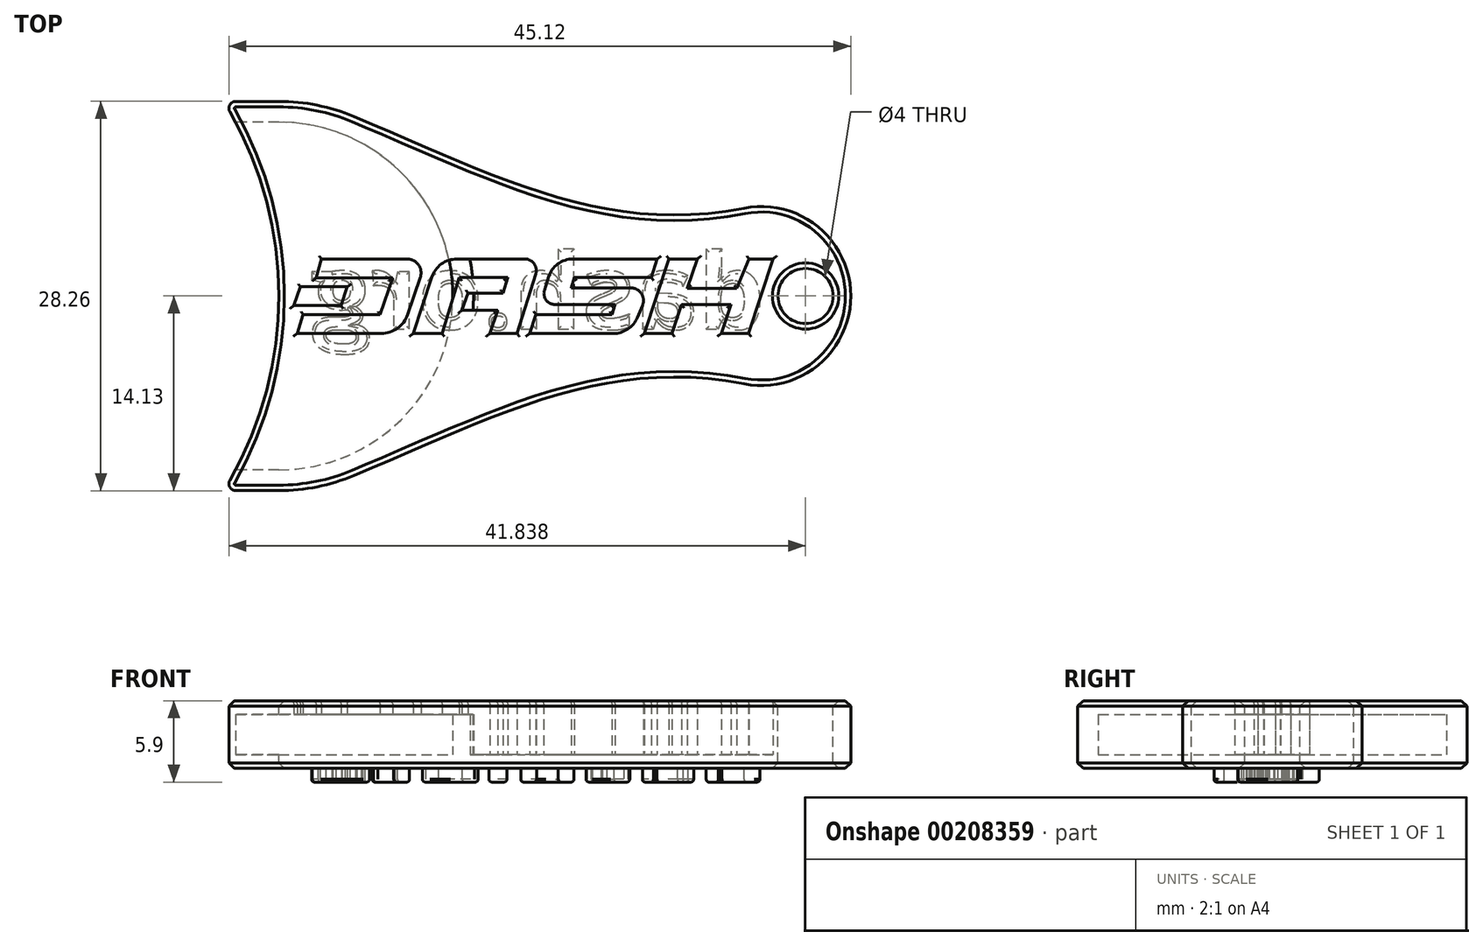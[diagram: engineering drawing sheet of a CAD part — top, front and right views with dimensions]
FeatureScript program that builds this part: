
annotation { "Feature Type Name" : "Feature", "Feature Type Description" : "" }
export const myFeature = defineFeature(function(context is Context, id is Id, definition is map)
    precondition{}
    {
        {
            var Q0;
            Q0=qCreatedBy(makeId("Top.planeOp"),FACE);
            var sketch = newSketch(context, id + "F0", { "sketchPlane" : qUnion([Q0])});
            skArc(sketch, "E0", {"start": v(0, -12.12) * mm, "mid": v(12.12, 0) * mm, "end": v(0, 12.12) * mm, "construction": true});
            skArc(sketch, "E1", {"start": v(0, -12.62) * mm, "mid": v(12.62, 0) * mm, "end": v(0, 12.62) * mm});
            skArc(sketch, "E2.0", {"start": v(0, -14.12) * mm, "mid": v(14.12, 0) * mm, "end": v(0, 14.12) * mm});
            skLineSegment(sketch, "E3", {"start": v(0, 15.93) * mm, "end": v(0, -15.93) * mm, "construction": true});
            skLineSegment(sketch, "E4", {"start": v(0, 14.12) * mm, "end": v(-3.12, 14.12) * mm});
            skLineSegment(sketch, "E5", {"start": v(0, -14.12) * mm, "end": v(-3.12, -14.12) * mm});
            skArc(sketch, "E6", {"start": v(-3.56, -13.38) * mm, "mid": v(0, 0) * mm, "end": v(-3.56, 13.38) * mm});
            skLineSegment(sketch, "E7", {"start": v(0, 12.62) * mm, "end": v(-3.14, 12.62) * mm});
            skLineSegment(sketch, "E8", {"start": v(0, -12.62) * mm, "end": v(-3.14, -12.62) * mm});
            skLineSegment(sketch, "E9", {"start": v(0, 0) * mm, "end": v(35, 0) * mm, "construction": true});
            skArc(sketch, "E10", {"start": v(33.74, -6.38) * mm, "mid": v(41.5, 0) * mm, "end": v(33.74, 6.38) * mm});
            skFitSpline(sketch, "E11", {"points": [v(33.74, 6.38) * mm, v(5.45, 13.03) * mm], "startDerivative": vector(-30.42, -5.99) * mm, "endDerivative": vector(-30.88, 12.92) * mm});
            skFitSpline(sketch, "E12.MirrorCS", {"points": [v(33.74, -6.38) * mm, v(5.45, -13.03) * mm], "startDerivative": vector(-30.42, 5.99) * mm, "endDerivative": vector(-30.88, -12.92) * mm});
            skCircle(sketch, "E13", {"center": v(38.22, 0) * mm, "radius": 2 * mm});
            skPoint(sketch, "E14.visualSharp", {"position": v(-4, 14.12) * mm});
            skArc(sketch, "E14.filletArc", {"start": v(-3.12, 14.12) * mm, "mid": v(-3.55, 13.88) * mm, "end": v(-3.56, 13.38) * mm});
            skPoint(sketch, "E15.visualSharp", {"position": v(-4, -14.12) * mm});
            skArc(sketch, "E15.filletArc", {"start": v(-3.56, -13.38) * mm, "mid": v(-3.55, -13.88) * mm, "end": v(-3.12, -14.12) * mm});
            skLineSegment(sketch, "E16", {"start": v(3.1, 2.69) * mm, "end": v(9.3, 2.69) * mm});
            skLineSegment(sketch, "E17", {"start": v(10.27, 1.35) * mm, "end": v(9.35, -1.34) * mm});
            skLineSegment(sketch, "E18", {"start": v(7.42, -2.72) * mm, "end": v(1.33, -2.72) * mm});
            skLineSegment(sketch, "E19", {"start": v(1.33, -2.72) * mm, "end": v(1.76, -1.34) * mm});
            skLineSegment(sketch, "E20", {"start": v(1.76, -1.34) * mm, "end": v(7.35, -1.34) * mm});
            skLineSegment(sketch, "E21", {"start": v(7.35, -1.34) * mm, "end": v(8.25, 1.3) * mm});
            skLineSegment(sketch, "E22", {"start": v(8.25, 1.3) * mm, "end": v(2.7, 1.3) * mm});
            skLineSegment(sketch, "E23", {"start": v(2.7, 1.3) * mm, "end": v(3.1, 2.69) * mm});
            skLineSegment(sketch, "E24", {"start": v(1.57, 0.67) * mm, "end": v(4.97, 0.67) * mm});
            skLineSegment(sketch, "E25", {"start": v(4.97, 0.67) * mm, "end": v(4.5, -0.7) * mm});
            skLineSegment(sketch, "E26", {"start": v(4.5, -0.7) * mm, "end": v(1.1, -0.7) * mm});
            skLineSegment(sketch, "E27", {"start": v(1.1, -0.7) * mm, "end": v(1.57, 0.67) * mm});
            skPoint(sketch, "E28.visualSharp", {"position": v(10.72, 2.69) * mm});
            skArc(sketch, "E28.filletArc", {"start": v(10.27, 1.35) * mm, "mid": v(10.13, 2.27) * mm, "end": v(9.3, 2.69) * mm});
            skPoint(sketch, "E29.visualSharp", {"position": v(8.88, -2.72) * mm});
            skArc(sketch, "E29.filletArc", {"start": v(7.42, -2.72) * mm, "mid": v(8.6, -2.34) * mm, "end": v(9.35, -1.34) * mm});
            skLineSegment(sketch, "E30", {"start": v(9.76, -2.72) * mm, "end": v(11.09, 1.35) * mm});
            skLineSegment(sketch, "E31", {"start": v(12.94, 2.69) * mm, "end": v(17.85, 2.69) * mm});
            skLineSegment(sketch, "E32", {"start": v(18.64, 1.61) * mm, "end": v(17.29, -2.72) * mm});
            skLineSegment(sketch, "E33", {"start": v(17.29, -2.72) * mm, "end": v(15.32, -2.72) * mm});
            skLineSegment(sketch, "E34", {"start": v(15.32, -2.72) * mm, "end": v(15.88, -1.04) * mm});
            skLineSegment(sketch, "E35", {"start": v(15.88, -1.04) * mm, "end": v(13.3, -1.04) * mm});
            skLineSegment(sketch, "E36", {"start": v(13.3, -1.04) * mm, "end": v(13.73, 0.21) * mm});
            skLineSegment(sketch, "E37", {"start": v(13.73, 0.21) * mm, "end": v(16.26, 0.21) * mm});
            skLineSegment(sketch, "E38", {"start": v(16.26, 0.21) * mm, "end": v(16.6, 1.34) * mm});
            skLineSegment(sketch, "E39", {"start": v(16.6, 1.34) * mm, "end": v(13.1, 1.34) * mm});
            skLineSegment(sketch, "E40", {"start": v(13.1, 1.34) * mm, "end": v(11.85, -2.72) * mm});
            skLineSegment(sketch, "E41", {"start": v(11.85, -2.72) * mm, "end": v(9.76, -2.72) * mm});
            skPoint(sketch, "E42.visualSharp", {"position": v(11.52, 2.69) * mm});
            skArc(sketch, "E42.filletArc", {"start": v(12.94, 2.69) * mm, "mid": v(11.8, 2.32) * mm, "end": v(11.09, 1.35) * mm});
            skPoint(sketch, "E43.visualSharp", {"position": v(18.98, 2.69) * mm});
            skArc(sketch, "E43.filletArc", {"start": v(18.64, 1.61) * mm, "mid": v(18.52, 2.35) * mm, "end": v(17.85, 2.69) * mm});
            skLineSegment(sketch, "E44", {"start": v(18.2, -2.72) * mm, "end": v(24.25, -2.72) * mm});
            skLineSegment(sketch, "E45", {"start": v(26.01, -1.56) * mm, "end": v(26.39, -0.69) * mm});
            skLineSegment(sketch, "E46", {"start": v(25.54, 0.6) * mm, "end": v(21.2, 0.6) * mm});
            skLineSegment(sketch, "E47", {"start": v(21.2, 0.6) * mm, "end": v(21.44, 1.33) * mm});
            skLineSegment(sketch, "E48", {"start": v(21.44, 1.33) * mm, "end": v(27.03, 1.33) * mm});
            skLineSegment(sketch, "E49", {"start": v(27.03, 1.33) * mm, "end": v(27.45, 2.69) * mm});
            skLineSegment(sketch, "E50", {"start": v(27.45, 2.69) * mm, "end": v(21.35, 2.69) * mm});
            skLineSegment(sketch, "E51", {"start": v(19.56, 1.38) * mm, "end": v(19.27, 0.43) * mm});
            skLineSegment(sketch, "E52", {"start": v(20.04, -0.61) * mm, "end": v(24.4, -0.61) * mm});
            skLineSegment(sketch, "E53", {"start": v(24.4, -0.61) * mm, "end": v(24.18, -1.34) * mm});
            skLineSegment(sketch, "E54", {"start": v(24.18, -1.34) * mm, "end": v(18.66, -1.34) * mm});
            skLineSegment(sketch, "E55", {"start": v(18.66, -1.34) * mm, "end": v(18.2, -2.72) * mm});
            skPoint(sketch, "E56.visualSharp", {"position": v(19.97, 2.69) * mm});
            skArc(sketch, "E56.filletArc", {"start": v(21.35, 2.69) * mm, "mid": v(20.24, 2.33) * mm, "end": v(19.56, 1.38) * mm});
            skPoint(sketch, "E57.visualSharp", {"position": v(18.94, -0.61) * mm});
            skArc(sketch, "E57.filletArc", {"start": v(19.27, 0.43) * mm, "mid": v(19.39, -0.28) * mm, "end": v(20.04, -0.61) * mm});
            skPoint(sketch, "E58.visualSharp", {"position": v(26.93, 0.6) * mm});
            skArc(sketch, "E58.filletArc", {"start": v(26.39, -0.69) * mm, "mid": v(26.3, 0.18) * mm, "end": v(25.54, 0.6) * mm});
            skPoint(sketch, "E59.visualSharp", {"position": v(25.52, -2.72) * mm});
            skArc(sketch, "E59.filletArc", {"start": v(24.25, -2.72) * mm, "mid": v(25.3, -2.4) * mm, "end": v(26.01, -1.56) * mm});
            skLineSegment(sketch, "E60", {"start": v(26.52, -2.72) * mm, "end": v(28.3, 2.69) * mm});
            skLineSegment(sketch, "E61", {"start": v(28.3, 2.69) * mm, "end": v(30.35, 2.69) * mm});
            skLineSegment(sketch, "E62", {"start": v(30.35, 2.69) * mm, "end": v(29.64, 0.57) * mm});
            skLineSegment(sketch, "E63", {"start": v(29.64, 0.57) * mm, "end": v(33.2, 0.57) * mm});
            skLineSegment(sketch, "E64", {"start": v(33.2, 0.57) * mm, "end": v(34.1, 2.69) * mm});
            skLineSegment(sketch, "E65", {"start": v(34.1, 2.69) * mm, "end": v(35.84, 2.69) * mm});
            skLineSegment(sketch, "E66", {"start": v(35.84, 2.69) * mm, "end": v(34.09, -2.72) * mm});
            skLineSegment(sketch, "E67", {"start": v(34.09, -2.72) * mm, "end": v(32.1, -2.72) * mm});
            skLineSegment(sketch, "E68", {"start": v(32.1, -2.72) * mm, "end": v(32.82, -0.64) * mm});
            skLineSegment(sketch, "E69", {"start": v(32.82, -0.64) * mm, "end": v(29.23, -0.64) * mm});
            skLineSegment(sketch, "E70", {"start": v(29.23, -0.64) * mm, "end": v(28.53, -2.72) * mm});
            skLineSegment(sketch, "E71", {"start": v(28.53, -2.72) * mm, "end": v(26.52, -2.72) * mm});
            skSolve(sketch);
        }
        {
            var Q0;
            {var subQ5=sQuery(id+"F0.wireOp",EDGE,"E7");Q0=makeQuery(id+"F0.imprint","IMPRINT",FACE,{"disambiguationData":[TD([[makeQuery(id+"F0.imprint","IMPRINT",EDGE,{"derivedFrom":subQ5}),1.0]])]});}
            var Q1;
            {var subQ4=sQuery(id+"F0.wireOp",EDGE,"E5");Q1=makeQuery(id+"F0.imprint","IMPRINT",FACE,{"disambiguationData":[TD([[makeQuery(id+"F0.imprint","IMPRINT",EDGE,{"derivedFrom":subQ4}),-1.0]])]});}
            var Q2;
            {var subQ5=sQuery(id+"F0.wireOp",EDGE,"E38");Q2=makeQuery(id+"F0.imprint","IMPRINT",FACE,{"disambiguationData":[TD([[makeQuery(id+"F0.imprint","IMPRINT",EDGE,{"derivedFrom":subQ5}),1.0]])]});}
            var Q3;
            {var subQ0=sQuery(id+"F0.wireOp",EDGE,"E4");Q3=makeQuery(id+"F0.imprint","IMPRINT",FACE,{"disambiguationData":[TD([[makeQuery(id+"F0.imprint","IMPRINT",EDGE,{"derivedFrom":subQ0}),1.0]])]});}
            var Q4;
            {var subQ5=sQuery(id+"F0.wireOp",EDGE,"E36");Q4=makeQuery(id+"F0.imprint","IMPRINT",FACE,{"disambiguationData":[TD([[makeQuery(id+"F0.imprint","IMPRINT",EDGE,{"derivedFrom":subQ5}),-1.0]])]});}
            var Q5;
            {var subQ6=sQuery(id+"F0.wireOp",EDGE,"E30");Q5=makeQuery(id+"F0.imprint","IMPRINT",FACE,{"disambiguationData":[TD([[makeQuery(id+"F0.imprint","IMPRINT",EDGE,{"derivedFrom":subQ6}),-1.0]])]});}
            var Q6;
            Q6=makeQuery(id+"F0.imprint","IMPRINT",FACE,{"disambiguationData":[TD([[makeQuery(id+"F0.imprint","IMPRINT",EDGE,{"derivedFrom":sQuery(id+"F0.wireOp",EDGE,"E32")}),-1.0]])]});
            var Q7;
            {var subQ0=sQuery(id+"F0.wireOp",EDGE,"E40");var subQ9=sQuery(id+"F0.wireOp",EDGE,"E1");var subQ10=makeQuery(id+"F0.imprint","INTERSECT",VERTEX,{"derivedFrom":[subQ9,subQ0]});Q7=makeQuery(id+"F0.imprint","IMPRINT",FACE,{"disambiguationData":[TD([[makeQuery(id+"F0.imprint","IMPRINT",EDGE,{"disambiguationData":[TD([[subQ10,-1.0]])],"derivedFrom":subQ9}),-1.0]])]});}
            var Q8;
            Q8=makeQuery(id+"F0.imprint","IMPRINT",FACE,{"disambiguationData":[TD([[makeQuery(id+"F0.imprint","IMPRINT",EDGE,{"derivedFrom":sQuery(id+"F0.wireOp",EDGE,"E10")}),1.0]])]});
            var Q9;
            Q9=makeQuery(id+"F0.imprint","IMPRINT",FACE,{"disambiguationData":[TD([[makeQuery(id+"F0.imprint","IMPRINT",EDGE,{"derivedFrom":sQuery(id+"F0.wireOp",EDGE,"E16")}),-1.0]])]});
            var Q10;
            Q10=makeQuery(id+"F0.imprint","IMPRINT",FACE,{"disambiguationData":[TD([[makeQuery(id+"F0.imprint","IMPRINT",EDGE,{"derivedFrom":sQuery(id+"F0.wireOp",EDGE,"E24")}),-1.0]])]});
            var Q11;
            Q11=makeQuery(id+"F0.imprint","IMPRINT",FACE,{"disambiguationData":[TD([[makeQuery(id+"F0.imprint","IMPRINT",EDGE,{"derivedFrom":sQuery(id+"F0.wireOp",EDGE,"E44")}),1.0]])]});
            var Q12;
            Q12=makeQuery(id+"F0.imprint","IMPRINT",FACE,{"disambiguationData":[TD([[makeQuery(id+"F0.imprint","IMPRINT",EDGE,{"derivedFrom":sQuery(id+"F0.wireOp",EDGE,"E60")}),-1.0]])]});
            extrude(context, id + "F1", {"entities" : qUnion([Q0, Q1, Q2, Q3, Q4, Q5, Q6, Q7, Q8, Q9, Q10, Q11, Q12]), "oppositeDirection" : true, "depth" : 1 * mm});
        }
        {
            var Q0;
            {var subQ0=sQuery(id+"F0.wireOp",EDGE,"E4");Q0=makeQuery(id+"F0.imprint","IMPRINT",FACE,{"disambiguationData":[TD([[makeQuery(id+"F0.imprint","IMPRINT",EDGE,{"derivedFrom":subQ0}),1.0]])]});}
            var Q1;
            {var subQ0=sQuery(id+"F0.wireOp",EDGE,"E40");var subQ9=sQuery(id+"F0.wireOp",EDGE,"E1");var subQ10=makeQuery(id+"F0.imprint","INTERSECT",VERTEX,{"derivedFrom":[subQ9,subQ0]});Q1=makeQuery(id+"F0.imprint","IMPRINT",FACE,{"disambiguationData":[TD([[makeQuery(id+"F0.imprint","IMPRINT",EDGE,{"disambiguationData":[TD([[subQ10,-1.0]])],"derivedFrom":subQ9}),-1.0]])]});}
            var Q2;
            {var subQ4=sQuery(id+"F0.wireOp",EDGE,"E5");Q2=makeQuery(id+"F0.imprint","IMPRINT",FACE,{"disambiguationData":[TD([[makeQuery(id+"F0.imprint","IMPRINT",EDGE,{"derivedFrom":subQ4}),-1.0]])]});}
            var Q3;
            {var subQ5=sQuery(id+"F0.wireOp",EDGE,"E36");Q3=makeQuery(id+"F0.imprint","IMPRINT",FACE,{"disambiguationData":[TD([[makeQuery(id+"F0.imprint","IMPRINT",EDGE,{"derivedFrom":subQ5}),-1.0]])]});}
            var Q4;
            Q4=makeQuery(id+"F0.imprint","IMPRINT",FACE,{"disambiguationData":[TD([[makeQuery(id+"F0.imprint","IMPRINT",EDGE,{"derivedFrom":sQuery(id+"F0.wireOp",EDGE,"E10")}),1.0]])]});
            var Q5;
            {var subQ5=sQuery(id+"F0.wireOp",EDGE,"E38");Q5=makeQuery(id+"F0.imprint","IMPRINT",FACE,{"disambiguationData":[TD([[makeQuery(id+"F0.imprint","IMPRINT",EDGE,{"derivedFrom":subQ5}),1.0]])]});}
            extrude(context, id + "F2", {"entities" : qUnion([Q0, Q1, Q2, Q3, Q4, Q5]), "operationType" : NewBodyOperationType.ADD, "depth" : 2.9 * mm});
        }
        {
            var Q0;
            Q0=makeQuery(id+"F2.opExtrude","CAP_FACE",FACE,{"disambiguationData":[OSD([sQuery(id+"F0.wireOp",EDGE,"E1"),sQuery(id+"F0.wireOp",EDGE,"E2.0"),sQuery(id+"F0.wireOp",EDGE,"E4"),sQuery(id+"F0.wireOp",EDGE,"E5"),sQuery(id+"F0.wireOp",EDGE,"E6"),sQuery(id+"F0.wireOp",EDGE,"E7"),sQuery(id+"F0.wireOp",EDGE,"E8"),sQuery(id+"F0.wireOp",EDGE,"E10"),sQuery(id+"F0.wireOp",EDGE,"E11"),sQuery(id+"F0.wireOp",EDGE,"E12.MirrorCS"),sQuery(id+"F0.wireOp",EDGE,"E13"),sQuery(id+"F0.wireOp",EDGE,"E14.filletArc"),sQuery(id+"F0.wireOp",EDGE,"E15.filletArc"),sQuery(id+"F0.wireOp",EDGE,"E31"),sQuery(id+"F0.wireOp",EDGE,"E32"),sQuery(id+"F0.wireOp",EDGE,"E33"),sQuery(id+"F0.wireOp",EDGE,"E34"),sQuery(id+"F0.wireOp",EDGE,"E35"),sQuery(id+"F0.wireOp",EDGE,"E37"),sQuery(id+"F0.wireOp",EDGE,"E38"),sQuery(id+"F0.wireOp",EDGE,"E39"),sQuery(id+"F0.wireOp",EDGE,"E43.filletArc"),sQuery(id+"F0.wireOp",EDGE,"E44"),sQuery(id+"F0.wireOp",EDGE,"E45"),sQuery(id+"F0.wireOp",EDGE,"E46"),sQuery(id+"F0.wireOp",EDGE,"E47"),sQuery(id+"F0.wireOp",EDGE,"E48"),sQuery(id+"F0.wireOp",EDGE,"E49"),sQuery(id+"F0.wireOp",EDGE,"E50"),sQuery(id+"F0.wireOp",EDGE,"E51"),sQuery(id+"F0.wireOp",EDGE,"E52"),sQuery(id+"F0.wireOp",EDGE,"E53"),sQuery(id+"F0.wireOp",EDGE,"E54"),sQuery(id+"F0.wireOp",EDGE,"E55"),sQuery(id+"F0.wireOp",EDGE,"E56.filletArc"),sQuery(id+"F0.wireOp",EDGE,"E57.filletArc"),sQuery(id+"F0.wireOp",EDGE,"E58.filletArc"),sQuery(id+"F0.wireOp",EDGE,"E59.filletArc"),sQuery(id+"F0.wireOp",EDGE,"E60"),sQuery(id+"F0.wireOp",EDGE,"E61"),sQuery(id+"F0.wireOp",EDGE,"E62"),sQuery(id+"F0.wireOp",EDGE,"E63"),sQuery(id+"F0.wireOp",EDGE,"E64"),sQuery(id+"F0.wireOp",EDGE,"E65"),sQuery(id+"F0.wireOp",EDGE,"E66"),sQuery(id+"F0.wireOp",EDGE,"E67"),sQuery(id+"F0.wireOp",EDGE,"E68"),sQuery(id+"F0.wireOp",EDGE,"E69"),sQuery(id+"F0.wireOp",EDGE,"E70"),sQuery(id+"F0.wireOp",EDGE,"E71")])],"isStart":false});
            var sketch = newSketch(context, id + "F3", { "sketchPlane" : qUnion([Q0])});
            skArc(sketch, "E72.0", {"start": v(-3.14, -12.62) * mm, "mid": v(0, 0) * mm, "end": v(-3.14, 12.62) * mm});
            skLineSegment(sketch, "E73.0.0", {"start": v(9.3, 2.69) * mm, "end": v(3.1, 2.69) * mm});
            skLineSegment(sketch, "E73.0.1", {"start": v(3.1, 2.69) * mm, "end": v(2.7, 1.3) * mm});
            skLineSegment(sketch, "E73.0.2", {"start": v(2.7, 1.3) * mm, "end": v(8.25, 1.3) * mm});
            skLineSegment(sketch, "E73.0.3", {"start": v(8.25, 1.3) * mm, "end": v(7.35, -1.34) * mm});
            skLineSegment(sketch, "E73.0.4", {"start": v(7.35, -1.34) * mm, "end": v(1.76, -1.34) * mm});
            skLineSegment(sketch, "E73.0.5", {"start": v(1.76, -1.34) * mm, "end": v(1.33, -2.72) * mm});
            skLineSegment(sketch, "E73.0.6", {"start": v(1.33, -2.72) * mm, "end": v(7.42, -2.72) * mm});
            skArc(sketch, "E73.0.7", {"start": v(7.42, -2.72) * mm, "mid": v(8.6, -2.34) * mm, "end": v(9.35, -1.34) * mm});
            skLineSegment(sketch, "E73.0.8", {"start": v(9.35, -1.34) * mm, "end": v(10.27, 1.35) * mm});
            skArc(sketch, "E73.0.9", {"start": v(10.27, 1.35) * mm, "mid": v(10.13, 2.27) * mm, "end": v(9.3, 2.69) * mm});
            skLineSegment(sketch, "E74.0.0", {"start": v(4.97, 0.67) * mm, "end": v(1.57, 0.67) * mm});
            skLineSegment(sketch, "E74.0.1", {"start": v(1.57, 0.67) * mm, "end": v(1.1, -0.7) * mm});
            skLineSegment(sketch, "E74.0.2", {"start": v(1.1, -0.7) * mm, "end": v(4.5, -0.7) * mm});
            skLineSegment(sketch, "E74.0.3", {"start": v(4.5, -0.7) * mm, "end": v(4.97, 0.67) * mm});
            skLineSegment(sketch, "E75.0.0", {"start": v(11.85, -2.72) * mm, "end": v(12.62, -0.2) * mm});
            skArc(sketch, "E75.0.1", {"start": v(12.62, -0.2) * mm, "mid": v(12.57, 1.2) * mm, "end": v(12.35, 2.6) * mm});
            skArc(sketch, "E75.0.2", {"start": v(12.35, 2.6) * mm, "mid": v(11.57, 2.13) * mm, "end": v(11.09, 1.35) * mm});
            skLineSegment(sketch, "E75.0.3", {"start": v(11.09, 1.35) * mm, "end": v(9.76, -2.72) * mm});
            skLineSegment(sketch, "E75.0.4", {"start": v(9.76, -2.72) * mm, "end": v(11.85, -2.72) * mm});
            skLineSegment(sketch, "E76.0", {"start": v(13.1, 1.34) * mm, "end": v(11.85, -2.72) * mm});
            skLineSegment(sketch, "E77.0", {"start": v(16.6, 1.34) * mm, "end": v(13.1, 1.34) * mm});
            skLineSegment(sketch, "E78.0", {"start": v(12.94, 2.69) * mm, "end": v(17.85, 2.69) * mm});
            skArc(sketch, "E79.0", {"start": v(12.94, 2.69) * mm, "mid": v(11.8, 2.32) * mm, "end": v(11.09, 1.35) * mm});
            skLineSegment(sketch, "E80.0", {"start": v(13.73, 0.21) * mm, "end": v(16.26, 0.21) * mm});
            skLineSegment(sketch, "E81.0", {"start": v(13.3, -1.04) * mm, "end": v(13.73, 0.21) * mm});
            skLineSegment(sketch, "E82.0", {"start": v(15.88, -1.04) * mm, "end": v(13.3, -1.04) * mm});
            skSolve(sketch);
        }
        {
            var Q0;
            Q0=makeQuery(id+"F3.imprint","IMPRINT",FACE,{"disambiguationData":[TD([[makeQuery(id+"F3.imprint","IMPRINT",EDGE,{"derivedFrom":sQuery(id+"F3.wireOp",EDGE,"E72.0")}),-1.0]])]});
            var Q1;
            {var subQ17=sQuery(id+"F3.wireOp",EDGE,"E81.0");Q1=makeQuery(id+"F3.imprint","IMPRINT",FACE,{"disambiguationData":[TD([[makeQuery(id+"F3.imprint","IMPRINT",EDGE,{"derivedFrom":subQ17}),1.0]])]});}
            extrude(context, id + "F4", {"entities" : qUnion([Q0, Q1]), "operationType" : NewBodyOperationType.ADD, "depth" : 1 * mm});
        }
        {
            var Q0;
            Q0=makeQuery(id+"F4.opExtrude","CAP_EDGE",EDGE,{"disambiguationData":[OSD([sQuery(id+"F0.wireOp",EDGE,"E13")])],"isStart":false});
            var Q1;
            Q1=makeQuery(id+"F1.opExtrude","CAP_EDGE",EDGE,{"disambiguationData":[OSD([sQuery(id+"F0.wireOp",EDGE,"E13")])],"isStart":false});
            var Q2;
            Q2=makeQuery(id+"F1.opExtrude","CAP_EDGE",EDGE,{"disambiguationData":[OSD([sQuery(id+"F0.wireOp",EDGE,"E12.MirrorCS")])],"isStart":false});
            var Q3;
            Q3=makeQuery(id+"F4.opExtrude","CAP_EDGE",EDGE,{"disambiguationData":[OSD([sQuery(id+"F0.wireOp",EDGE,"E12.MirrorCS")])],"isStart":false});
            chamfer(context, id + "F5", {"entities" : qUnion([Q0, Q1, Q2, Q3]), "width" : .4 * mm, "tangentPropagation" : true});
        }
        {
            var Q0;
            Q0=makeQuery(id+"F4.opExtrude","CAP_EDGE",EDGE,{"disambiguationData":[OSD([sQuery(id+"F3.wireOp",EDGE,"E73.0.0")])],"isStart":false});
            var Q1;
            Q1=makeQuery(id+"F4.opExtrude","CAP_EDGE",EDGE,{"disambiguationData":[OSD([sQuery(id+"F3.wireOp",EDGE,"E73.0.2")])],"isStart":false});
            var Q2;
            Q2=makeQuery(id+"F4.opExtrude","CAP_EDGE",EDGE,{"disambiguationData":[OSD([sQuery(id+"F3.wireOp",EDGE,"E73.0.4")])],"isStart":false});
            var Q3;
            Q3=makeQuery(id+"F4.opExtrude","CAP_EDGE",EDGE,{"disambiguationData":[OSD([sQuery(id+"F3.wireOp",EDGE,"E73.0.5")])],"isStart":false});
            var Q4;
            Q4=makeQuery(id+"F4.opExtrude","CAP_EDGE",EDGE,{"disambiguationData":[OSD([sQuery(id+"F3.wireOp",EDGE,"E73.0.1")])],"isStart":false});
            var Q5;
            Q5=makeQuery(id+"F4.opExtrude","CAP_EDGE",EDGE,{"disambiguationData":[OSD([sQuery(id+"F3.wireOp",EDGE,"E73.0.3")])],"isStart":false});
            var Q6;
            Q6=makeQuery(id+"F4.opExtrude","CAP_EDGE",EDGE,{"disambiguationData":[OSD([sQuery(id+"F3.wireOp",EDGE,"E74.0.0")])],"isStart":false});
            var Q7;
            Q7=makeQuery(id+"F4.opExtrude","CAP_EDGE",EDGE,{"disambiguationData":[OSD([sQuery(id+"F3.wireOp",EDGE,"E74.0.2")])],"isStart":false});
            var Q8;
            Q8=makeQuery(id+"F4.opExtrude","CAP_EDGE",EDGE,{"disambiguationData":[OSD([sQuery(id+"F3.wireOp",EDGE,"E74.0.3")])],"isStart":false});
            var Q9;
            Q9=makeQuery(id+"F4.opExtrude","CAP_EDGE",EDGE,{"disambiguationData":[OSD([sQuery(id+"F3.wireOp",EDGE,"E74.0.1")])],"isStart":false});
            var Q10;
            Q10=makeQuery(id+"F4.opExtrude","CAP_EDGE",EDGE,{"disambiguationData":[OSD([sQuery(id+"F3.wireOp",EDGE,"E78.0")])],"isStart":false});
            var Q11;
            Q11=makeQuery(id+"F4.opExtrude","CAP_EDGE",EDGE,{"disambiguationData":[OSD([sQuery(id+"F3.wireOp",EDGE,"E77.0")])],"isStart":false});
            var Q12;
            Q12=makeQuery(id+"F4.opExtrude","CAP_EDGE",EDGE,{"disambiguationData":[OSD([sQuery(id+"F3.wireOp",EDGE,"E80.0")])],"isStart":false});
            var Q13;
            Q13=makeQuery(id+"F4.opExtrude","CAP_EDGE",EDGE,{"disambiguationData":[OSD([sQuery(id+"F0.wireOp",EDGE,"E38")])],"isStart":false});
            var Q14;
            Q14=makeQuery(id+"F4.opExtrude","CAP_EDGE",EDGE,{"disambiguationData":[OSD([sQuery(id+"F3.wireOp",EDGE,"E81.0")])],"isStart":false});
            var Q15;
            Q15=makeQuery(id+"F4.opExtrude","CAP_EDGE",EDGE,{"disambiguationData":[OSD([sQuery(id+"F3.wireOp",EDGE,"E82.0")])],"isStart":false});
            var Q16;
            Q16=makeQuery(id+"F4.opExtrude","CAP_EDGE",EDGE,{"disambiguationData":[OSD([sQuery(id+"F0.wireOp",EDGE,"E34")])],"isStart":false});
            var Q17;
            Q17=makeQuery(id+"F4.opExtrude","CAP_EDGE",EDGE,{"disambiguationData":[OSD([sQuery(id+"F0.wireOp",EDGE,"E33")])],"isStart":false});
            var Q18;
            Q18=makeQuery(id+"F4.opExtrude","CAP_EDGE",EDGE,{"disambiguationData":[OSD([sQuery(id+"F3.wireOp",EDGE,"E75.0.4")])],"isStart":false});
            var Q19;
            Q19=makeQuery(id+"F4.opExtrude","CAP_EDGE",EDGE,{"disambiguationData":[OSD([sQuery(id+"F3.wireOp",EDGE,"E76.0")])],"isStart":false});
            var Q20;
            Q20=makeQuery(id+"F4.opExtrude","CAP_EDGE",EDGE,{"disambiguationData":[OSD([sQuery(id+"F0.wireOp",EDGE,"E50")])],"isStart":false});
            var Q21;
            Q21=makeQuery(id+"F4.opExtrude","CAP_EDGE",EDGE,{"disambiguationData":[OSD([sQuery(id+"F0.wireOp",EDGE,"E46")])],"isStart":false});
            var Q22;
            Q22=makeQuery(id+"F4.opExtrude","CAP_EDGE",EDGE,{"disambiguationData":[OSD([sQuery(id+"F0.wireOp",EDGE,"E48")])],"isStart":false});
            var Q23;
            Q23=makeQuery(id+"F4.opExtrude","CAP_EDGE",EDGE,{"disambiguationData":[OSD([sQuery(id+"F0.wireOp",EDGE,"E49")])],"isStart":false});
            var Q24;
            Q24=makeQuery(id+"F4.opExtrude","CAP_EDGE",EDGE,{"disambiguationData":[OSD([sQuery(id+"F0.wireOp",EDGE,"E47")])],"isStart":false});
            var Q25;
            Q25=makeQuery(id+"F4.opExtrude","CAP_EDGE",EDGE,{"disambiguationData":[OSD([sQuery(id+"F0.wireOp",EDGE,"E53")])],"isStart":false});
            var Q26;
            Q26=makeQuery(id+"F4.opExtrude","CAP_EDGE",EDGE,{"disambiguationData":[OSD([sQuery(id+"F0.wireOp",EDGE,"E55")])],"isStart":false});
            var Q27;
            Q27=makeQuery(id+"F4.opExtrude","CAP_EDGE",EDGE,{"disambiguationData":[OSD([sQuery(id+"F0.wireOp",EDGE,"E54")])],"isStart":false});
            var Q28;
            Q28=makeQuery(id+"F4.opExtrude","CAP_EDGE",EDGE,{"disambiguationData":[OSD([sQuery(id+"F0.wireOp",EDGE,"E60")])],"isStart":false});
            var Q29;
            Q29=makeQuery(id+"F4.opExtrude","CAP_EDGE",EDGE,{"disambiguationData":[OSD([sQuery(id+"F0.wireOp",EDGE,"E63")])],"isStart":false});
            var Q30;
            Q30=makeQuery(id+"F4.opExtrude","CAP_EDGE",EDGE,{"disambiguationData":[OSD([sQuery(id+"F0.wireOp",EDGE,"E69")])],"isStart":false});
            var Q31;
            Q31=makeQuery(id+"F4.opExtrude","CAP_EDGE",EDGE,{"disambiguationData":[OSD([sQuery(id+"F0.wireOp",EDGE,"E65")])],"isStart":false});
            var Q32;
            Q32=makeQuery(id+"F4.opExtrude","CAP_EDGE",EDGE,{"disambiguationData":[OSD([sQuery(id+"F0.wireOp",EDGE,"E64")])],"isStart":false});
            var Q33;
            Q33=makeQuery(id+"F4.opExtrude","CAP_EDGE",EDGE,{"disambiguationData":[OSD([sQuery(id+"F0.wireOp",EDGE,"E66")])],"isStart":false});
            var Q34;
            Q34=makeQuery(id+"F4.opExtrude","CAP_EDGE",EDGE,{"disambiguationData":[OSD([sQuery(id+"F0.wireOp",EDGE,"E67")])],"isStart":false});
            var Q35;
            Q35=makeQuery(id+"F4.opExtrude","CAP_EDGE",EDGE,{"disambiguationData":[OSD([sQuery(id+"F0.wireOp",EDGE,"E71")])],"isStart":false});
            var Q36;
            Q36=makeQuery(id+"F4.opExtrude","CAP_EDGE",EDGE,{"disambiguationData":[OSD([sQuery(id+"F0.wireOp",EDGE,"E61")])],"isStart":false});
            var Q37;
            Q37=makeQuery(id+"F4.opExtrude","CAP_EDGE",EDGE,{"disambiguationData":[OSD([sQuery(id+"F0.wireOp",EDGE,"E70")])],"isStart":false});
            var Q38;
            Q38=makeQuery(id+"F4.opExtrude","CAP_EDGE",EDGE,{"disambiguationData":[OSD([sQuery(id+"F0.wireOp",EDGE,"E62")])],"isStart":false});
            var Q39;
            Q39=makeQuery(id+"F4.opExtrude","CAP_EDGE",EDGE,{"disambiguationData":[OSD([sQuery(id+"F0.wireOp",EDGE,"E68")])],"isStart":false});
            fillet(context, id + "F6", {"entities" : qUnion([Q0, Q1, Q2, Q3, Q4, Q5, Q6, Q7, Q8, Q9, Q10, Q11, Q12, Q13, Q14, Q15, Q16, Q17, Q18, Q19, Q20, Q21, Q22, Q23, Q24, Q25, Q26, Q27, Q28, Q29, Q30, Q31, Q32, Q33, Q34, Q35, Q36, Q37, Q38, Q39]), "radius" : .2 * mm, "tangentPropagation" : true, "allowEdgeOverflow" : false});
        }
        {
            var Q0;
            Q0=makeQuery(id+"F1.opExtrude","CAP_FACE",FACE,{"disambiguationData":[OSD([sQuery(id+"F0.wireOp",EDGE,"E2.0"),sQuery(id+"F0.wireOp",EDGE,"E4"),sQuery(id+"F0.wireOp",EDGE,"E5"),sQuery(id+"F0.wireOp",EDGE,"E6"),sQuery(id+"F0.wireOp",EDGE,"E10"),sQuery(id+"F0.wireOp",EDGE,"E11"),sQuery(id+"F0.wireOp",EDGE,"E12.MirrorCS"),sQuery(id+"F0.wireOp",EDGE,"E13"),sQuery(id+"F0.wireOp",EDGE,"E14.filletArc"),sQuery(id+"F0.wireOp",EDGE,"E15.filletArc")])],"isStart":false});
            var sketch = newSketch(context, id + "F7", { "sketchPlane" : qUnion([Q0])});
            skText(sketch, "E83", { "text": "dash.org", "fontName": "OpenSans-Bold.ttf"});
            const initialGuessF7  = {"E83": [0.03525, 0.0024, -1, 0, 0.0055]};
            skSetInitialGuess(sketch, initialGuessF7);
            skSolve(sketch);
        }
        {
            var Q0;
            Q0 = qSketchRegion(id + "F7", true);
            extrude(context, id + "F8", {"entities" : qUnion([Q0]), "operationType" : NewBodyOperationType.ADD, "depth" : 1 * mm});
        }
        {
            var Q0;
            Q0=makeQuery(id+"F8.opExtrude","CAP_FACE",FACE,{"disambiguationData":[OSD([sQuery(id+"F7.wireOp",EDGE,"E83.sketch_text.stroke-0"),sQuery(id+"F7.wireOp",EDGE,"E83.sketch_text.stroke-1"),sQuery(id+"F7.wireOp",EDGE,"E83.sketch_text.stroke-2"),sQuery(id+"F7.wireOp",EDGE,"E83.sketch_text.stroke-3"),sQuery(id+"F7.wireOp",EDGE,"E83.sketch_text.stroke-4"),sQuery(id+"F7.wireOp",EDGE,"E83.sketch_text.stroke-5"),sQuery(id+"F7.wireOp",EDGE,"E83.sketch_text.stroke-6"),sQuery(id+"F7.wireOp",EDGE,"E83.sketch_text.stroke-7"),sQuery(id+"F7.wireOp",EDGE,"E83.sketch_text.stroke-8"),sQuery(id+"F7.wireOp",EDGE,"E83.sketch_text.stroke-9"),sQuery(id+"F7.wireOp",EDGE,"E83.sketch_text.stroke-10"),sQuery(id+"F7.wireOp",EDGE,"E83.sketch_text.stroke-11"),sQuery(id+"F7.wireOp",EDGE,"E83.sketch_text.stroke-12"),sQuery(id+"F7.wireOp",EDGE,"E83.sketch_text.stroke-13"),sQuery(id+"F7.wireOp",EDGE,"E83.sketch_text.stroke-14"),sQuery(id+"F7.wireOp",EDGE,"E83.sketch_text.stroke-15"),sQuery(id+"F7.wireOp",EDGE,"E83.sketch_text.stroke-16"),sQuery(id+"F7.wireOp",EDGE,"E83.sketch_text.stroke-17"),sQuery(id+"F7.wireOp",EDGE,"E83.sketch_text.stroke-18"),sQuery(id+"F7.wireOp",EDGE,"E83.sketch_text.stroke-19"),sQuery(id+"F7.wireOp",EDGE,"E83.sketch_text.stroke-20"),sQuery(id+"F7.wireOp",EDGE,"E83.sketch_text.stroke-21"),sQuery(id+"F7.wireOp",EDGE,"E83.sketch_text.stroke-22")])],"isStart":false});
            var Q1;
            Q1=makeQuery(id+"F8.opExtrude","CAP_FACE",FACE,{"disambiguationData":[OSD([sQuery(id+"F7.wireOp",EDGE,"E83.sketch_text.stroke-23"),sQuery(id+"F7.wireOp",EDGE,"E83.sketch_text.stroke-24"),sQuery(id+"F7.wireOp",EDGE,"E83.sketch_text.stroke-25"),sQuery(id+"F7.wireOp",EDGE,"E83.sketch_text.stroke-26"),sQuery(id+"F7.wireOp",EDGE,"E83.sketch_text.stroke-27"),sQuery(id+"F7.wireOp",EDGE,"E83.sketch_text.stroke-28"),sQuery(id+"F7.wireOp",EDGE,"E83.sketch_text.stroke-29"),sQuery(id+"F7.wireOp",EDGE,"E83.sketch_text.stroke-30"),sQuery(id+"F7.wireOp",EDGE,"E83.sketch_text.stroke-31"),sQuery(id+"F7.wireOp",EDGE,"E83.sketch_text.stroke-32"),sQuery(id+"F7.wireOp",EDGE,"E83.sketch_text.stroke-33"),sQuery(id+"F7.wireOp",EDGE,"E83.sketch_text.stroke-34"),sQuery(id+"F7.wireOp",EDGE,"E83.sketch_text.stroke-35"),sQuery(id+"F7.wireOp",EDGE,"E83.sketch_text.stroke-36"),sQuery(id+"F7.wireOp",EDGE,"E83.sketch_text.stroke-37"),sQuery(id+"F7.wireOp",EDGE,"E83.sketch_text.stroke-38"),sQuery(id+"F7.wireOp",EDGE,"E83.sketch_text.stroke-39"),sQuery(id+"F7.wireOp",EDGE,"E83.sketch_text.stroke-40"),sQuery(id+"F7.wireOp",EDGE,"E83.sketch_text.stroke-41"),sQuery(id+"F7.wireOp",EDGE,"E83.sketch_text.stroke-42"),sQuery(id+"F7.wireOp",EDGE,"E83.sketch_text.stroke-43"),sQuery(id+"F7.wireOp",EDGE,"E83.sketch_text.stroke-44"),sQuery(id+"F7.wireOp",EDGE,"E83.sketch_text.stroke-45"),sQuery(id+"F7.wireOp",EDGE,"E83.sketch_text.stroke-46"),sQuery(id+"F7.wireOp",EDGE,"E83.sketch_text.stroke-47")])],"isStart":false});
            var Q2;
            Q2=makeQuery(id+"F8.opExtrude","CAP_FACE",FACE,{"disambiguationData":[OSD([sQuery(id+"F7.wireOp",EDGE,"E83.sketch_text.stroke-48"),sQuery(id+"F7.wireOp",EDGE,"E83.sketch_text.stroke-49"),sQuery(id+"F7.wireOp",EDGE,"E83.sketch_text.stroke-50"),sQuery(id+"F7.wireOp",EDGE,"E83.sketch_text.stroke-51"),sQuery(id+"F7.wireOp",EDGE,"E83.sketch_text.stroke-52"),sQuery(id+"F7.wireOp",EDGE,"E83.sketch_text.stroke-53"),sQuery(id+"F7.wireOp",EDGE,"E83.sketch_text.stroke-54"),sQuery(id+"F7.wireOp",EDGE,"E83.sketch_text.stroke-55"),sQuery(id+"F7.wireOp",EDGE,"E83.sketch_text.stroke-56"),sQuery(id+"F7.wireOp",EDGE,"E83.sketch_text.stroke-57"),sQuery(id+"F7.wireOp",EDGE,"E83.sketch_text.stroke-58"),sQuery(id+"F7.wireOp",EDGE,"E83.sketch_text.stroke-59"),sQuery(id+"F7.wireOp",EDGE,"E83.sketch_text.stroke-60"),sQuery(id+"F7.wireOp",EDGE,"E83.sketch_text.stroke-61"),sQuery(id+"F7.wireOp",EDGE,"E83.sketch_text.stroke-62"),sQuery(id+"F7.wireOp",EDGE,"E83.sketch_text.stroke-63"),sQuery(id+"F7.wireOp",EDGE,"E83.sketch_text.stroke-64"),sQuery(id+"F7.wireOp",EDGE,"E83.sketch_text.stroke-65"),sQuery(id+"F7.wireOp",EDGE,"E83.sketch_text.stroke-66"),sQuery(id+"F7.wireOp",EDGE,"E83.sketch_text.stroke-67"),sQuery(id+"F7.wireOp",EDGE,"E83.sketch_text.stroke-68"),sQuery(id+"F7.wireOp",EDGE,"E83.sketch_text.stroke-69"),sQuery(id+"F7.wireOp",EDGE,"E83.sketch_text.stroke-70"),sQuery(id+"F7.wireOp",EDGE,"E83.sketch_text.stroke-71"),sQuery(id+"F7.wireOp",EDGE,"E83.sketch_text.stroke-72"),sQuery(id+"F7.wireOp",EDGE,"E83.sketch_text.stroke-73")])],"isStart":false});
            var Q3;
            Q3=makeQuery(id+"F8.opExtrude","CAP_FACE",FACE,{"disambiguationData":[OSD([sQuery(id+"F7.wireOp",EDGE,"E83.sketch_text.stroke-74"),sQuery(id+"F7.wireOp",EDGE,"E83.sketch_text.stroke-75"),sQuery(id+"F7.wireOp",EDGE,"E83.sketch_text.stroke-76"),sQuery(id+"F7.wireOp",EDGE,"E83.sketch_text.stroke-77"),sQuery(id+"F7.wireOp",EDGE,"E83.sketch_text.stroke-78"),sQuery(id+"F7.wireOp",EDGE,"E83.sketch_text.stroke-79"),sQuery(id+"F7.wireOp",EDGE,"E83.sketch_text.stroke-80"),sQuery(id+"F7.wireOp",EDGE,"E83.sketch_text.stroke-81"),sQuery(id+"F7.wireOp",EDGE,"E83.sketch_text.stroke-82"),sQuery(id+"F7.wireOp",EDGE,"E83.sketch_text.stroke-83"),sQuery(id+"F7.wireOp",EDGE,"E83.sketch_text.stroke-84"),sQuery(id+"F7.wireOp",EDGE,"E83.sketch_text.stroke-85"),sQuery(id+"F7.wireOp",EDGE,"E83.sketch_text.stroke-86"),sQuery(id+"F7.wireOp",EDGE,"E83.sketch_text.stroke-87"),sQuery(id+"F7.wireOp",EDGE,"E83.sketch_text.stroke-88"),sQuery(id+"F7.wireOp",EDGE,"E83.sketch_text.stroke-89"),sQuery(id+"F7.wireOp",EDGE,"E83.sketch_text.stroke-90")])],"isStart":false});
            var Q4;
            Q4=makeQuery(id+"F8.opExtrude","CAP_FACE",FACE,{"disambiguationData":[OSD([sQuery(id+"F7.wireOp",EDGE,"E83.sketch_text.stroke-91"),sQuery(id+"F7.wireOp",EDGE,"E83.sketch_text.stroke-92"),sQuery(id+"F7.wireOp",EDGE,"E83.sketch_text.stroke-93"),sQuery(id+"F7.wireOp",EDGE,"E83.sketch_text.stroke-94"),sQuery(id+"F7.wireOp",EDGE,"E83.sketch_text.stroke-95"),sQuery(id+"F7.wireOp",EDGE,"E83.sketch_text.stroke-96"),sQuery(id+"F7.wireOp",EDGE,"E83.sketch_text.stroke-97"),sQuery(id+"F7.wireOp",EDGE,"E83.sketch_text.stroke-98")])],"isStart":false});
            var Q5;
            Q5=makeQuery(id+"F8.opExtrude","CAP_FACE",FACE,{"disambiguationData":[OSD([sQuery(id+"F7.wireOp",EDGE,"E83.sketch_text.stroke-99"),sQuery(id+"F7.wireOp",EDGE,"E83.sketch_text.stroke-100"),sQuery(id+"F7.wireOp",EDGE,"E83.sketch_text.stroke-101"),sQuery(id+"F7.wireOp",EDGE,"E83.sketch_text.stroke-102"),sQuery(id+"F7.wireOp",EDGE,"E83.sketch_text.stroke-103"),sQuery(id+"F7.wireOp",EDGE,"E83.sketch_text.stroke-104"),sQuery(id+"F7.wireOp",EDGE,"E83.sketch_text.stroke-105"),sQuery(id+"F7.wireOp",EDGE,"E83.sketch_text.stroke-106"),sQuery(id+"F7.wireOp",EDGE,"E83.sketch_text.stroke-107"),sQuery(id+"F7.wireOp",EDGE,"E83.sketch_text.stroke-108"),sQuery(id+"F7.wireOp",EDGE,"E83.sketch_text.stroke-109"),sQuery(id+"F7.wireOp",EDGE,"E83.sketch_text.stroke-110"),sQuery(id+"F7.wireOp",EDGE,"E83.sketch_text.stroke-111"),sQuery(id+"F7.wireOp",EDGE,"E83.sketch_text.stroke-112"),sQuery(id+"F7.wireOp",EDGE,"E83.sketch_text.stroke-113"),sQuery(id+"F7.wireOp",EDGE,"E83.sketch_text.stroke-114"),sQuery(id+"F7.wireOp",EDGE,"E83.sketch_text.stroke-115"),sQuery(id+"F7.wireOp",EDGE,"E83.sketch_text.stroke-116")])],"isStart":false});
            var Q6;
            Q6=makeQuery(id+"F8.opExtrude","CAP_FACE",FACE,{"disambiguationData":[OSD([sQuery(id+"F7.wireOp",EDGE,"E83.sketch_text.stroke-117"),sQuery(id+"F7.wireOp",EDGE,"E83.sketch_text.stroke-118"),sQuery(id+"F7.wireOp",EDGE,"E83.sketch_text.stroke-119"),sQuery(id+"F7.wireOp",EDGE,"E83.sketch_text.stroke-120"),sQuery(id+"F7.wireOp",EDGE,"E83.sketch_text.stroke-121"),sQuery(id+"F7.wireOp",EDGE,"E83.sketch_text.stroke-122"),sQuery(id+"F7.wireOp",EDGE,"E83.sketch_text.stroke-123"),sQuery(id+"F7.wireOp",EDGE,"E83.sketch_text.stroke-124"),sQuery(id+"F7.wireOp",EDGE,"E83.sketch_text.stroke-125"),sQuery(id+"F7.wireOp",EDGE,"E83.sketch_text.stroke-126"),sQuery(id+"F7.wireOp",EDGE,"E83.sketch_text.stroke-127"),sQuery(id+"F7.wireOp",EDGE,"E83.sketch_text.stroke-128"),sQuery(id+"F7.wireOp",EDGE,"E83.sketch_text.stroke-129")])],"isStart":false});
            var Q7;
            Q7=makeQuery(id+"F8.opExtrude","CAP_FACE",FACE,{"disambiguationData":[OSD([sQuery(id+"F7.wireOp",EDGE,"E83.sketch_text.stroke-130"),sQuery(id+"F7.wireOp",EDGE,"E83.sketch_text.stroke-131"),sQuery(id+"F7.wireOp",EDGE,"E83.sketch_text.stroke-132"),sQuery(id+"F7.wireOp",EDGE,"E83.sketch_text.stroke-133"),sQuery(id+"F7.wireOp",EDGE,"E83.sketch_text.stroke-134"),sQuery(id+"F7.wireOp",EDGE,"E83.sketch_text.stroke-135"),sQuery(id+"F7.wireOp",EDGE,"E83.sketch_text.stroke-136"),sQuery(id+"F7.wireOp",EDGE,"E83.sketch_text.stroke-137"),sQuery(id+"F7.wireOp",EDGE,"E83.sketch_text.stroke-138"),sQuery(id+"F7.wireOp",EDGE,"E83.sketch_text.stroke-139"),sQuery(id+"F7.wireOp",EDGE,"E83.sketch_text.stroke-140"),sQuery(id+"F7.wireOp",EDGE,"E83.sketch_text.stroke-141"),sQuery(id+"F7.wireOp",EDGE,"E83.sketch_text.stroke-142"),sQuery(id+"F7.wireOp",EDGE,"E83.sketch_text.stroke-143"),sQuery(id+"F7.wireOp",EDGE,"E83.sketch_text.stroke-144"),sQuery(id+"F7.wireOp",EDGE,"E83.sketch_text.stroke-145"),sQuery(id+"F7.wireOp",EDGE,"E83.sketch_text.stroke-146"),sQuery(id+"F7.wireOp",EDGE,"E83.sketch_text.stroke-147"),sQuery(id+"F7.wireOp",EDGE,"E83.sketch_text.stroke-148"),sQuery(id+"F7.wireOp",EDGE,"E83.sketch_text.stroke-149"),sQuery(id+"F7.wireOp",EDGE,"E83.sketch_text.stroke-150"),sQuery(id+"F7.wireOp",EDGE,"E83.sketch_text.stroke-151"),sQuery(id+"F7.wireOp",EDGE,"E83.sketch_text.stroke-152"),sQuery(id+"F7.wireOp",EDGE,"E83.sketch_text.stroke-153"),sQuery(id+"F7.wireOp",EDGE,"E83.sketch_text.stroke-154"),sQuery(id+"F7.wireOp",EDGE,"E83.sketch_text.stroke-155"),sQuery(id+"F7.wireOp",EDGE,"E83.sketch_text.stroke-156"),sQuery(id+"F7.wireOp",EDGE,"E83.sketch_text.stroke-157"),sQuery(id+"F7.wireOp",EDGE,"E83.sketch_text.stroke-158"),sQuery(id+"F7.wireOp",EDGE,"E83.sketch_text.stroke-159"),sQuery(id+"F7.wireOp",EDGE,"E83.sketch_text.stroke-160"),sQuery(id+"F7.wireOp",EDGE,"E83.sketch_text.stroke-161"),sQuery(id+"F7.wireOp",EDGE,"E83.sketch_text.stroke-162"),sQuery(id+"F7.wireOp",EDGE,"E83.sketch_text.stroke-163"),sQuery(id+"F7.wireOp",EDGE,"E83.sketch_text.stroke-164"),sQuery(id+"F7.wireOp",EDGE,"E83.sketch_text.stroke-165"),sQuery(id+"F7.wireOp",EDGE,"E83.sketch_text.stroke-166"),sQuery(id+"F7.wireOp",EDGE,"E83.sketch_text.stroke-167"),sQuery(id+"F7.wireOp",EDGE,"E83.sketch_text.stroke-168"),sQuery(id+"F7.wireOp",EDGE,"E83.sketch_text.stroke-169"),sQuery(id+"F7.wireOp",EDGE,"E83.sketch_text.stroke-170"),sQuery(id+"F7.wireOp",EDGE,"E83.sketch_text.stroke-171"),sQuery(id+"F7.wireOp",EDGE,"E83.sketch_text.stroke-172"),sQuery(id+"F7.wireOp",EDGE,"E83.sketch_text.stroke-173")])],"isStart":false});
            fillet(context, id + "F9", {"entities" : qUnion([Q0, Q1, Q2, Q3, Q4, Q5, Q6, Q7]), "radius" : .2 * mm, "tangentPropagation" : true, "allowEdgeOverflow" : false});
        }
    });
